# Revit family: nightmatic_5000-3_011697
name_source: partatom
category: Elektroinstallationen
revit_build: Autodesk Revit 2016 (Build: 20190508_0715(x64)
units: mm (PartAtom-declared; Revit-internal decimal feet)

## family parameters
Basisbauteil = Fläche
Beim Laden mit Abzugskörper schneiden = Nein
Bemaßung runder Anschluss = Durchmesser verwenden
Beschriftungsausrichtung beibehalten = Nein
Gemeinsam genutzt = Nein
Raumberechnungspunkt = Nein
Teiletyp = Normal

## types (1)
- NightMatic 5000-3
    Apparent Load = 0 VA
    Beschreibung = Type: Photo-cell controller; Dimensions (L x W x H): 42 x 95 x 95 mm; Mains power supply: 220 – 240 V / 50 – 60 Hz; Sensor Technology: Light sensor; Application, place: Indoors; Installation site: wall, corner; Installation: Surface wiring; Twilight setting: 2 – 1000 lx; Switching output 1, resistive: 2000 W; Switching output 1, number of LEDs / fluorescent lamps: 8 pcs.; Basic light level function: No; Functions: Night economy mode, light ON / OFF in the morning; Settings via: Remote control, Potentiometers, Smart Remote; IP-rating: IP54; Material: Plastic; Ambient temperature: -20 – 50 °C; Colour: white; Colour, RAL: 9003; Manufacturer's Warranty: 5 years; Version: COM1 - white; PU1, EAN: 4007841011697
    Height = 95 mm
    Hersteller = Steinel
    Length = 42 mm
    ModVariant = Nein
    Modell = 011697
    Mounting Type = Surface mounted
    Number of Poles = 1
    OnlyDefault = Ja
    Power Factor = 1
    Product Name = NightMatic 5000-3
    Product group = Sensor-switched indoor light
    ProductGroupID = 30
    Protection Class = Protection class
    Protection Degree = IP 54
    RlxData = <blob elided: 20589 chars, md5=e1b188cf>
    SensorDataFile = {"IESDataFiles":[]}
    Typenbild = produkt1_011697.jpg
    Typenkommentare = Product without accessories
    URL = http://relux.com
    VarID = ---
    Voltage = 0 V
    Vorgabe-Ansicht = 1800 mm
    Weight = 0.00 kg
    Width = 95 mm

## geometry (parser evidence)
native form markers: Blend x4, Sweep x13
no freeform markers — native parametric forms only
